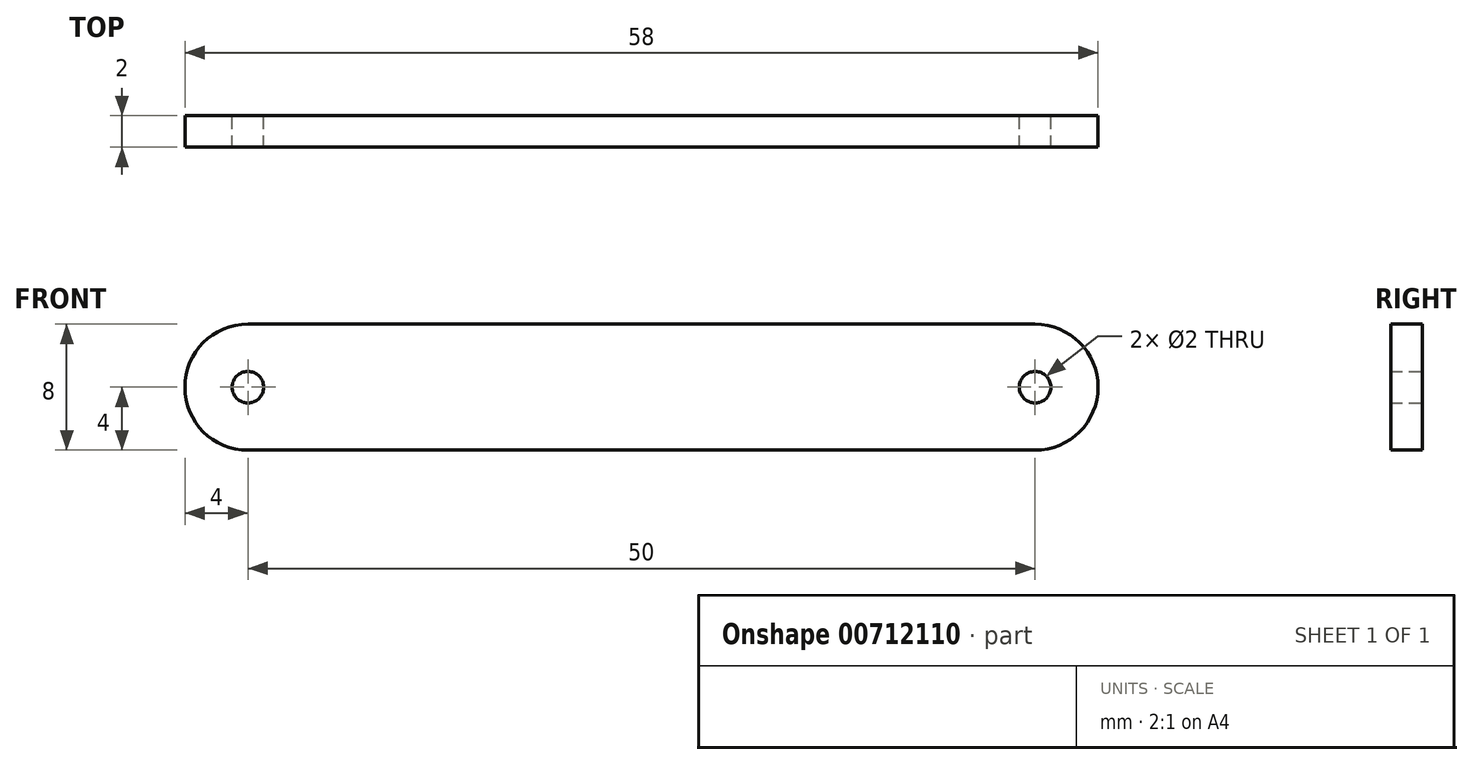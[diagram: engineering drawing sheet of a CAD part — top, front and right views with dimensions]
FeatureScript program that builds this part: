
annotation { "Feature Type Name" : "Feature", "Feature Type Description" : "" }
export const myFeature = defineFeature(function(context is Context, id is Id, definition is map)
    precondition{}
    {
        {
            var Q0;
            Q0=qCreatedBy(makeId("Front.planeOp"),FACE);
            var sketch = newSketch(context, id + "F0", { "sketchPlane" : qUnion([Q0])});
            skLineSegment(sketch, "E0.bottom", {"start": v(25, -4) * mm, "end": v(-25, -4) * mm});
            skLineSegment(sketch, "E0.top", {"start": v(25, 4) * mm, "end": v(-25, 4) * mm});
            skLineSegment(sketch, "E0.left", {"start": v(25, -4) * mm, "end": v(25, 4) * mm, "construction": true});
            skLineSegment(sketch, "E0.right", {"start": v(-25, -4) * mm, "end": v(-25, 4) * mm, "construction": true});
            skPoint(sketch, "E0.middle", {"position": v(0, 0) * mm});
            skArc(sketch, "E1", {"start": v(25, -4) * mm, "mid": v(29, 0) * mm, "end": v(25, 4) * mm});
            skArc(sketch, "E2", {"start": v(-25, 4) * mm, "mid": v(-29, 0) * mm, "end": v(-25, -4) * mm});
            skCircle(sketch, "E3", {"center": v(25, 0) * mm, "radius": 1 * mm});
            skCircle(sketch, "E4", {"center": v(-25, 0) * mm, "radius": 1 * mm});
            skSolve(sketch);
        }
        {
            var Q0;
            Q0 = qSketchRegion(id + "F0", true);
            extrude(context, id + "F1", {"entities" : qUnion([Q0]), "depth" : 2 * mm, "offsetDistance" : 25 * mm});
        }
    });
